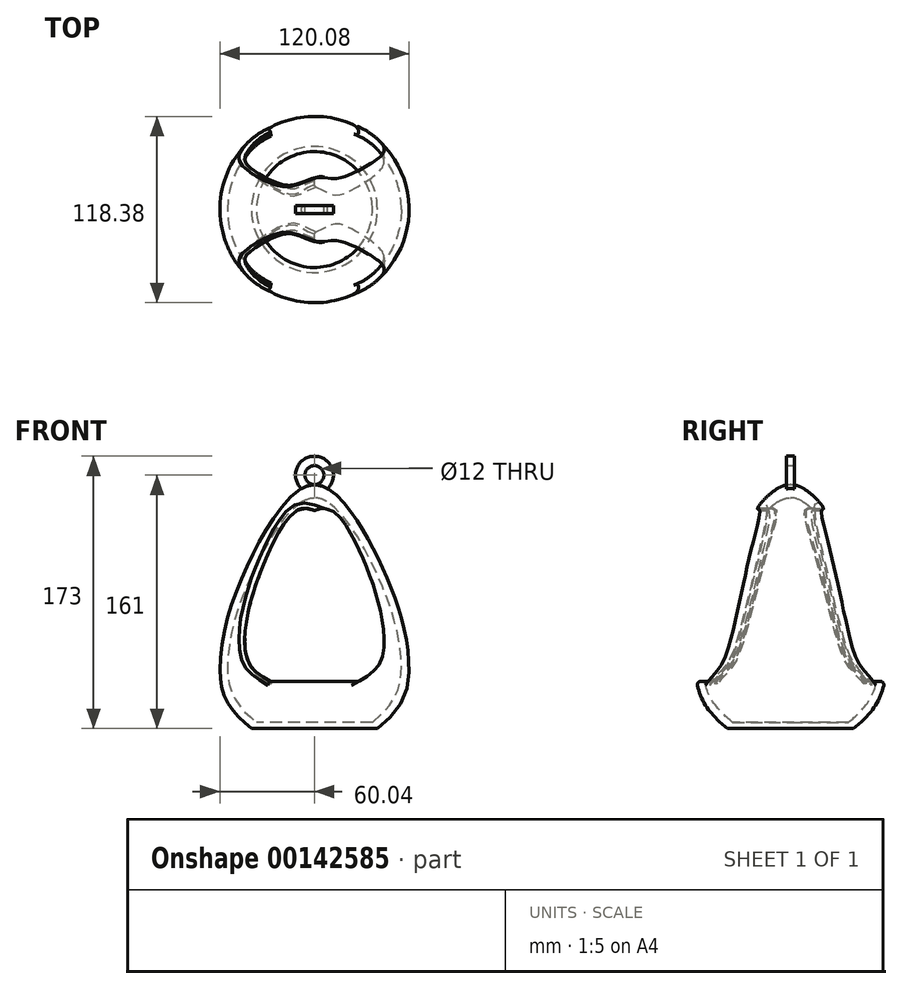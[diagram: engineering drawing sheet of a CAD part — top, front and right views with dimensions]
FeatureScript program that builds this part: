
annotation { "Feature Type Name" : "Feature", "Feature Type Description" : "" }
export const myFeature = defineFeature(function(context is Context, id is Id, definition is map)
    precondition{}
    {
        {
            var Q0;
            Q0=qCreatedBy(makeId("Front.planeOp"),FACE);
            var sketch = newSketch(context, id + "F0", { "sketchPlane" : qUnion([Q0])});
            skLineSegment(sketch, "E0", {"start": v(0, 0) * mm, "end": v(-40, 0) * mm});
            skFitSpline(sketch, "E1", {"points": [v(-40, 0) * mm, v(-60, 40) * mm, v(-45.59, 96.87) * mm, v(0, 155) * mm], "startDerivative": vector(-185.14, 146.52) * mm, "endDerivative": vector(127.65, -1.36) * mm});
            skLineSegment(sketch, "E2", {"start": v(0, 155) * mm, "end": v(0, 0) * mm});
            skArc(sketch, "E3", {"start": v(0, 149) * mm, "mid": v(-12, 161) * mm, "end": v(0, 173) * mm});
            skArc(sketch, "E4", {"start": v(0, 155) * mm, "mid": v(-6, 161) * mm, "end": v(0, 167) * mm});
            skLineSegment(sketch, "E5", {"start": v(0, 167) * mm, "end": v(0, 173) * mm});
            skSolve(sketch);
        }
        {
            var Q0;
            Q0=makeQuery(id+"F0.imprint","IMPRINT",FACE,{"disambiguationData":[TD([[makeQuery(id+"F0.imprint","IMPRINT",EDGE,{"derivedFrom":sQuery(id+"F0.wireOp",EDGE,"E0")}),-1.0]])]});
            var Q1;
            {var subQ0=sQuery(id+"F0.wireOp",EDGE,"E3");var subQ1=sQuery(id+"F0.wireOp",EDGE,"E1");var subQ2=makeQuery(id+"F0.imprint","INTERSECT",VERTEX,{"derivedFrom":[subQ1,subQ0]});Q1=makeQuery(id+"F0.imprint","IMPRINT",FACE,{"disambiguationData":[TD([[makeQuery(id+"F0.imprint","IMPRINT",EDGE,{"disambiguationData":[TD([[subQ2,-1.0]])],"derivedFrom":subQ1}),-1.0]])]});}
            var Q2;
            Q2=sQuery(id+"F0.wireOp",EDGE,"E2");
            revolve(context, id + "F1", {"entities" : qUnion([Q0, Q1]), "axis" : qUnion([Q2]), "revolveType" : RevolveType.FULL});
        }
        {
            var Q0;
            Q0=makeQuery(id+"F1.opRevolve","SWEPT_BODY",BODY,{"disambiguationData":[OSD([sQuery(id+"F0.wireOp",EDGE,"E0"),sQuery(id+"F0.wireOp",EDGE,"E1"),sQuery(id+"F0.wireOp",EDGE,"E2")])]});
            var Q1;
            Q1=qCreatedBy(makeId("Origin.pointOp"),VERTEX);
            transform(context, id + "F2", {"entities" : qUnion([Q0]), "transformType" : TransformType.SCALE_UNIFORMLY, "scale" : 0.92, "scalePoint" : qUnion([Q1]), "makeCopy" : true});
        }
        {
            var Q0;
            Q0=makeQuery(id+"F2.opPattern","COPY",BODY,{"derivedFrom":makeQuery(id+"F1.opRevolve","SWEPT_BODY",BODY,{"disambiguationData":[OSD([sQuery(id+"F0.wireOp",EDGE,"E0"),sQuery(id+"F0.wireOp",EDGE,"E1"),sQuery(id+"F0.wireOp",EDGE,"E2")])]}),"instanceName":"1"});
            transform(context, id + "F3", {"entities" : qUnion([Q0]), "transformType" : TransformType.TRANSLATION_3D, "dx" : 0 * mm, "dy" : 0 * mm, "dz" : 4 * mm, "makeCopy" : false});
        }
        {
            var Q0;
            Q0=makeQuery(id+"F2.opPattern","COPY",BODY,{"derivedFrom":makeQuery(id+"F1.opRevolve","SWEPT_BODY",BODY,{"disambiguationData":[OSD([sQuery(id+"F0.wireOp",EDGE,"E0"),sQuery(id+"F0.wireOp",EDGE,"E1"),sQuery(id+"F0.wireOp",EDGE,"E2")])]}),"instanceName":"1"});
            var Q1;
            Q1=makeQuery(id+"F1.opRevolve","SWEPT_BODY",BODY,{"disambiguationData":[OSD([sQuery(id+"F0.wireOp",EDGE,"E0"),sQuery(id+"F0.wireOp",EDGE,"E1"),sQuery(id+"F0.wireOp",EDGE,"E2")])]});
            booleanBodies(context, id + "F4", {"operationType" : BooleanOperationType.SUBTRACTION, "tools" : qUnion([Q0]), "targets" : qUnion([Q1])});
        }
        {
            var Q0;
            Q0=qCreatedBy(makeId("Front.planeOp"),FACE);
            var sketch = newSketch(context, id + "F5", { "sketchPlane" : qUnion([Q0])});
            skFitSpline(sketch, "E6.0", {"points": [v(-40, 0) * mm, v(-57.99, 14.24) * mm, v(-63.11, 40.02) * mm, v(-50.95, 93.97) * mm, v(-15.94, 155.17) * mm, v(0, 155) * mm]});
            skLineSegment(sketch, "E7.0", {"start": v(0, 0) * mm, "end": v(-40, 0) * mm});
            skLineSegment(sketch, "E8.0", {"start": v(0, 155) * mm, "end": v(0, 0) * mm, "construction": true});
            skLineSegment(sketch, "E9.MirrorCS", {"start": v(0, 0) * mm, "end": v(40, 0) * mm});
            skFitSpline(sketch, "E10.MirrorCS", {"points": [v(40, 0) * mm, v(57.99, 14.24) * mm, v(63.11, 40.02) * mm, v(50.95, 93.97) * mm, v(15.94, 155.17) * mm, v(0, 155) * mm]});
            skFitSpline(sketch, "E11.MirrorCS", {"points": [v(40, 0) * mm, v(57.99, 14.24) * mm, v(63.11, 40.02) * mm, v(50.95, 93.97) * mm, v(15.94, 155.17) * mm, v(0, 155) * mm]});
            skSolve(sketch);
        }
        {
            var Q0;
            Q0=makeQuery(id+"F5.imprint","IMPRINT",FACE,{"disambiguationData":[TD([[makeQuery(id+"F5.imprint","IMPRINT",EDGE,{"derivedFrom":sQuery(id+"F5.wireOp",EDGE,"E6.0")}),-1.0]])]});
            extrude(context, id + "F6", {"entities" : qUnion([Q0]), "endBound" : BoundingType.SYMMETRIC, "depth" : 200 * mm});
        }
        {
            var Q0;
            Q0=makeQuery(id+"F6.opExtrude","SWEPT_BODY",BODY,{"disambiguationData":[OSD([sQuery(id+"F5.wireOp",EDGE,"E6.0"),sQuery(id+"F5.wireOp",EDGE,"E7.0"),sQuery(id+"F5.wireOp",EDGE,"E9.MirrorCS"),sQuery(id+"F5.wireOp",EDGE,"E11.MirrorCS")])]});
            var Q1;
            Q1=qCreatedBy(makeId("Origin.pointOp"),VERTEX);
            transform(context, id + "F7", {"entities" : qUnion([Q0]), "transformType" : TransformType.SCALE_UNIFORMLY, "scale" : 0.7, "scalePoint" : qUnion([Q1]), "makeCopy" : false});
        }
        {
            var Q0;
            Q0=makeQuery(id+"F6.opExtrude","SWEPT_BODY",BODY,{"disambiguationData":[OSD([sQuery(id+"F5.wireOp",EDGE,"E6.0"),sQuery(id+"F5.wireOp",EDGE,"E7.0"),sQuery(id+"F5.wireOp",EDGE,"E9.MirrorCS"),sQuery(id+"F5.wireOp",EDGE,"E11.MirrorCS")])]});
            transform(context, id + "F8", {"entities" : qUnion([Q0]), "transformType" : TransformType.TRANSLATION_3D, "dx" : 0 * mm, "dy" : 0 * mm, "dz" : 30 * mm, "makeCopy" : false});
        }
        {
            var Q0;
            Q0=makeQuery(id+"F6.opExtrude","SWEPT_BODY",BODY,{"disambiguationData":[OSD([sQuery(id+"F5.wireOp",EDGE,"E6.0"),sQuery(id+"F5.wireOp",EDGE,"E7.0"),sQuery(id+"F5.wireOp",EDGE,"E9.MirrorCS"),sQuery(id+"F5.wireOp",EDGE,"E11.MirrorCS")])]});
            var Q1;
            Q1=makeQuery(id+"F1.opRevolve","SWEPT_BODY",BODY,{"disambiguationData":[OSD([sQuery(id+"F0.wireOp",EDGE,"E0"),sQuery(id+"F0.wireOp",EDGE,"E1"),sQuery(id+"F0.wireOp",EDGE,"E2")])]});
            booleanBodies(context, id + "F9", {"operationType" : BooleanOperationType.SUBTRACTION, "tools" : qUnion([Q0]), "targets" : qUnion([Q1])});
        }
        {
            var Q0;
            Q0=makeQuery(id+"F9.opBoolean","INTERSECT",EDGE,{"disambiguationData":[OD(0.0)],"derivedFrom":[makeQuery(id+"F1.opRevolve","SWEPT_FACE",FACE,{"disambiguationData":[OSD([sQuery(id+"F0.wireOp",EDGE,"E1")])]}),makeQuery(id+"F6.opExtrude","SWEPT_FACE",FACE,{"disambiguationData":[OSD([sQuery(id+"F5.wireOp",EDGE,"E7.0"),sQuery(id+"F5.wireOp",EDGE,"E9.MirrorCS")])]})]});
            var Q1;
            Q1=makeQuery(id+"F9.opBoolean","INTERSECT",EDGE,{"disambiguationData":[OD(0.0)],"derivedFrom":[makeQuery(id+"F1.opRevolve","SWEPT_FACE",FACE,{"disambiguationData":[OSD([sQuery(id+"F0.wireOp",EDGE,"E1")])]}),makeQuery(id+"F6.opExtrude","SWEPT_FACE",FACE,{"disambiguationData":[OSD([sQuery(id+"F5.wireOp",EDGE,"E11.MirrorCS")])]})]});
            var Q2;
            Q2=makeQuery(id+"F9.opBoolean","INTERSECT",EDGE,{"disambiguationData":[OD(0.0)],"derivedFrom":[makeQuery(id+"F1.opRevolve","SWEPT_FACE",FACE,{"disambiguationData":[OSD([sQuery(id+"F0.wireOp",EDGE,"E1")])]}),makeQuery(id+"F6.opExtrude","SWEPT_FACE",FACE,{"disambiguationData":[OSD([sQuery(id+"F5.wireOp",EDGE,"E6.0")])]})]});
            var Q3;
            Q3=makeQuery(id+"F9.opBoolean","INTERSECT",EDGE,{"disambiguationData":[OD(0.0)],"derivedFrom":[makeQuery(id+"F4.opBoolean","COPY",FACE,{"derivedFrom":makeQuery(id+"F2.opPattern","COPY",FACE,{"derivedFrom":makeQuery(id+"F1.opRevolve","SWEPT_FACE",FACE,{"disambiguationData":[OSD([sQuery(id+"F0.wireOp",EDGE,"E1")])]}),"instanceName":"1"})}),makeQuery(id+"F6.opExtrude","SWEPT_FACE",FACE,{"disambiguationData":[OSD([sQuery(id+"F5.wireOp",EDGE,"E7.0"),sQuery(id+"F5.wireOp",EDGE,"E9.MirrorCS")])]})]});
            var Q4;
            Q4=makeQuery(id+"F9.opBoolean","INTERSECT",EDGE,{"disambiguationData":[OD(0.0)],"derivedFrom":[makeQuery(id+"F4.opBoolean","COPY",FACE,{"derivedFrom":makeQuery(id+"F2.opPattern","COPY",FACE,{"derivedFrom":makeQuery(id+"F1.opRevolve","SWEPT_FACE",FACE,{"disambiguationData":[OSD([sQuery(id+"F0.wireOp",EDGE,"E1")])]}),"instanceName":"1"})}),makeQuery(id+"F6.opExtrude","SWEPT_FACE",FACE,{"disambiguationData":[OSD([sQuery(id+"F5.wireOp",EDGE,"E11.MirrorCS")])]})]});
            var Q5;
            Q5=makeQuery(id+"F9.opBoolean","INTERSECT",EDGE,{"disambiguationData":[OD(0.0)],"derivedFrom":[makeQuery(id+"F4.opBoolean","COPY",FACE,{"derivedFrom":makeQuery(id+"F2.opPattern","COPY",FACE,{"derivedFrom":makeQuery(id+"F1.opRevolve","SWEPT_FACE",FACE,{"disambiguationData":[OSD([sQuery(id+"F0.wireOp",EDGE,"E1")])]}),"instanceName":"1"})}),makeQuery(id+"F6.opExtrude","SWEPT_FACE",FACE,{"disambiguationData":[OSD([sQuery(id+"F5.wireOp",EDGE,"E6.0")])]})]});
            var Q6;
            Q6=makeQuery(id+"F9.opBoolean","INTERSECT",EDGE,{"disambiguationData":[OD(1.0)],"derivedFrom":[makeQuery(id+"F1.opRevolve","SWEPT_FACE",FACE,{"disambiguationData":[OSD([sQuery(id+"F0.wireOp",EDGE,"E1")])]}),makeQuery(id+"F6.opExtrude","SWEPT_FACE",FACE,{"disambiguationData":[OSD([sQuery(id+"F5.wireOp",EDGE,"E7.0"),sQuery(id+"F5.wireOp",EDGE,"E9.MirrorCS")])]})]});
            var Q7;
            Q7=makeQuery(id+"F9.opBoolean","INTERSECT",EDGE,{"disambiguationData":[OD(1.0)],"derivedFrom":[makeQuery(id+"F4.opBoolean","COPY",FACE,{"derivedFrom":makeQuery(id+"F2.opPattern","COPY",FACE,{"derivedFrom":makeQuery(id+"F1.opRevolve","SWEPT_FACE",FACE,{"disambiguationData":[OSD([sQuery(id+"F0.wireOp",EDGE,"E1")])]}),"instanceName":"1"})}),makeQuery(id+"F6.opExtrude","SWEPT_FACE",FACE,{"disambiguationData":[OSD([sQuery(id+"F5.wireOp",EDGE,"E7.0"),sQuery(id+"F5.wireOp",EDGE,"E9.MirrorCS")])]})]});
            var Q8;
            Q8=makeQuery(id+"F9.opBoolean","INTERSECT",EDGE,{"disambiguationData":[OD(1.0)],"derivedFrom":[makeQuery(id+"F4.opBoolean","COPY",FACE,{"derivedFrom":makeQuery(id+"F2.opPattern","COPY",FACE,{"derivedFrom":makeQuery(id+"F1.opRevolve","SWEPT_FACE",FACE,{"disambiguationData":[OSD([sQuery(id+"F0.wireOp",EDGE,"E1")])]}),"instanceName":"1"})}),makeQuery(id+"F6.opExtrude","SWEPT_FACE",FACE,{"disambiguationData":[OSD([sQuery(id+"F5.wireOp",EDGE,"E11.MirrorCS")])]})]});
            var Q9;
            Q9=makeQuery(id+"F9.opBoolean","INTERSECT",EDGE,{"disambiguationData":[OD(1.0)],"derivedFrom":[makeQuery(id+"F1.opRevolve","SWEPT_FACE",FACE,{"disambiguationData":[OSD([sQuery(id+"F0.wireOp",EDGE,"E1")])]}),makeQuery(id+"F6.opExtrude","SWEPT_FACE",FACE,{"disambiguationData":[OSD([sQuery(id+"F5.wireOp",EDGE,"E11.MirrorCS")])]})]});
            var Q10;
            Q10=makeQuery(id+"F9.opBoolean","INTERSECT",EDGE,{"disambiguationData":[OD(1.0)],"derivedFrom":[makeQuery(id+"F1.opRevolve","SWEPT_FACE",FACE,{"disambiguationData":[OSD([sQuery(id+"F0.wireOp",EDGE,"E1")])]}),makeQuery(id+"F6.opExtrude","SWEPT_FACE",FACE,{"disambiguationData":[OSD([sQuery(id+"F5.wireOp",EDGE,"E6.0")])]})]});
            var Q11;
            Q11=makeQuery(id+"F9.opBoolean","INTERSECT",EDGE,{"disambiguationData":[OD(1.0)],"derivedFrom":[makeQuery(id+"F4.opBoolean","COPY",FACE,{"derivedFrom":makeQuery(id+"F2.opPattern","COPY",FACE,{"derivedFrom":makeQuery(id+"F1.opRevolve","SWEPT_FACE",FACE,{"disambiguationData":[OSD([sQuery(id+"F0.wireOp",EDGE,"E1")])]}),"instanceName":"1"})}),makeQuery(id+"F6.opExtrude","SWEPT_FACE",FACE,{"disambiguationData":[OSD([sQuery(id+"F5.wireOp",EDGE,"E6.0")])]})]});
            fillet(context, id + "F10", {"entities" : qUnion([Q0, Q1, Q2, Q3, Q4, Q5, Q6, Q7, Q8, Q9, Q10, Q11]), "radius" : 2.1 * mm, "tangentPropagation" : true, "allowEdgeOverflow" : false});
        }
        {
            var Q0;
            {var subQ5=sQuery(id+"F0.wireOp",EDGE,"E5");Q0=makeQuery(id+"F0.imprint","IMPRINT",FACE,{"disambiguationData":[TD([[makeQuery(id+"F0.imprint","IMPRINT",EDGE,{"derivedFrom":subQ5}),1.0]])]});}
            var Q1;
            {var subQ0=sQuery(id+"F0.wireOp",EDGE,"E3");var subQ1=sQuery(id+"F0.wireOp",EDGE,"E1");var subQ2=makeQuery(id+"F0.imprint","INTERSECT",VERTEX,{"derivedFrom":[subQ1,subQ0]});Q1=makeQuery(id+"F0.imprint","IMPRINT",FACE,{"disambiguationData":[TD([[makeQuery(id+"F0.imprint","IMPRINT",EDGE,{"disambiguationData":[TD([[subQ2,-1.0]])],"derivedFrom":subQ1}),-1.0]])]});}
            extrude(context, id + "F11", {"entities" : qUnion([Q0, Q1]), "endBound" : BoundingType.SYMMETRIC, "depth" : 5 * mm});
        }
        {
            var Q0;
            Q0=makeQuery(id+"F11.opExtrude","SWEPT_BODY",BODY,{"disambiguationData":[OSD([sQuery(id+"F0.wireOp",EDGE,"E2"),sQuery(id+"F0.wireOp",EDGE,"E3"),sQuery(id+"F0.wireOp",EDGE,"E4"),sQuery(id+"F0.wireOp",EDGE,"E5")])]});
            var Q1;
            Q1=makeQuery(id+"F11.opExtrude","SWEPT_FACE",FACE,{"disambiguationData":[OSD([sQuery(id+"F0.wireOp",EDGE,"E2")])]});
            mirror(context, id + "F12", {"operationType" : NewBodyOperationType.ADD, "entities" : qUnion([Q0]), "mirrorPlane" : qUnion([Q1])});
        }
    });
